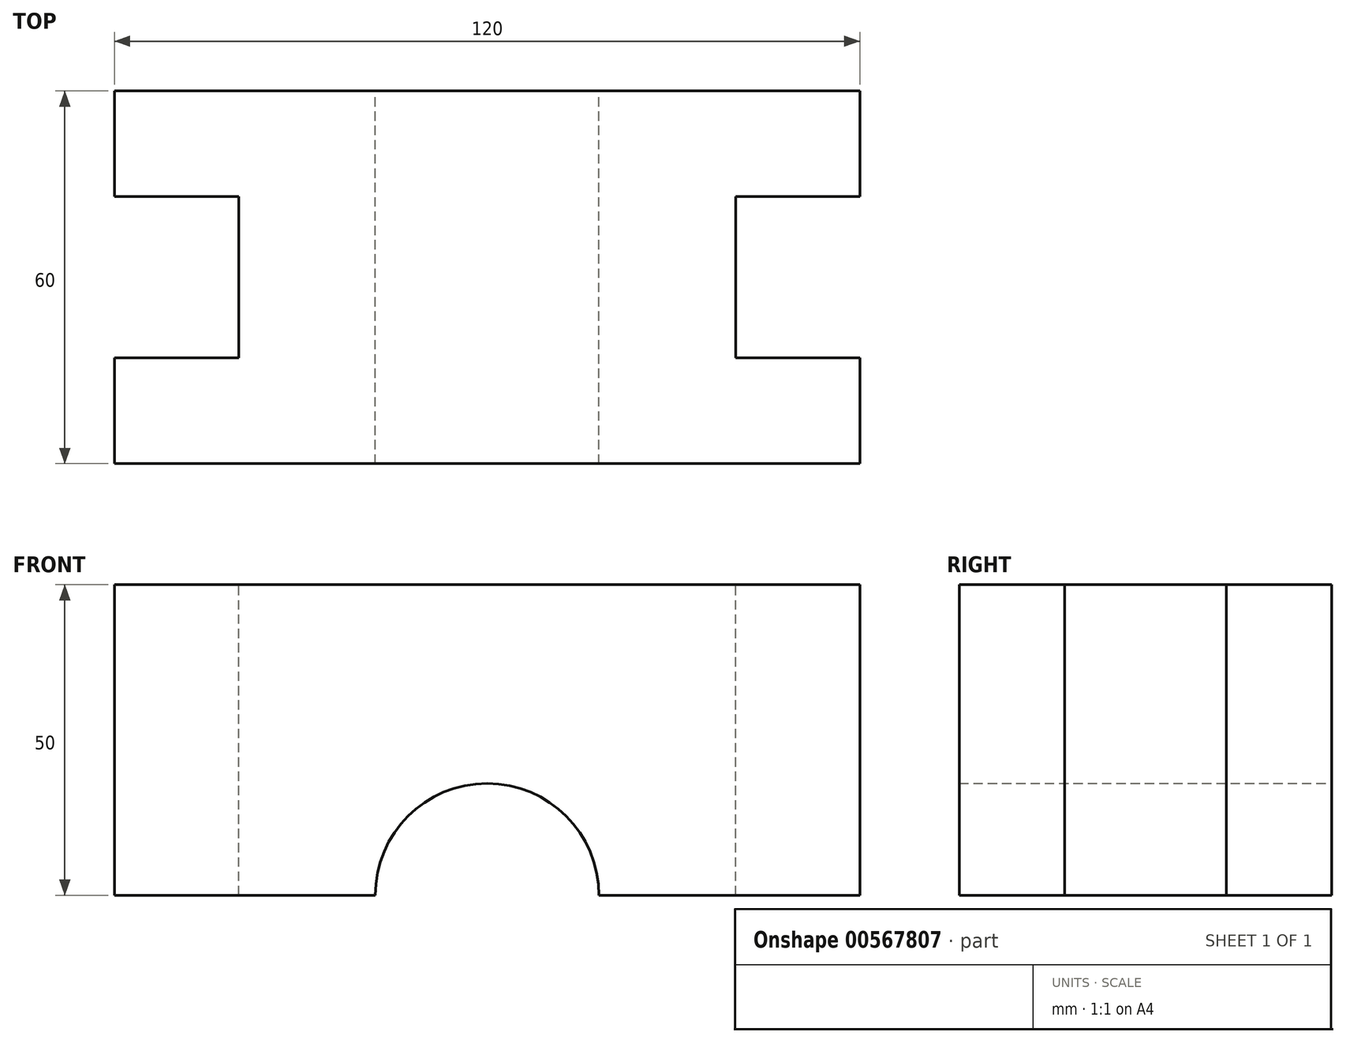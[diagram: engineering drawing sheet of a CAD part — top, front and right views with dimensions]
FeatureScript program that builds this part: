
annotation { "Feature Type Name" : "Feature", "Feature Type Description" : "" }
export const myFeature = defineFeature(function(context is Context, id is Id, definition is map)
    precondition{}
    {
        {
            var Q0;
            Q0=qCreatedBy(makeId("Front.planeOp"),FACE);
            var sketch = newSketch(context, id + "F0", { "sketchPlane" : qUnion([Q0])});
            skLineSegment(sketch, "E0.bottom", {"start": v(-60, 25) * mm, "end": v(60, 25) * mm});
            skLineSegment(sketch, "E0.top", {"start": v(-60, -25) * mm, "end": v(-18, -25) * mm});
            skLineSegment(sketch, "E0.left", {"start": v(-60, 25) * mm, "end": v(-60, -25) * mm});
            skLineSegment(sketch, "E0.right", {"start": v(60, 25) * mm, "end": v(60, -25) * mm});
            skPoint(sketch, "E0.middle", {"position": v(0, 0) * mm});
            skArc(sketch, "E1", {"start": v(18, -25) * mm, "mid": v(0, -7) * mm, "end": v(-18, -25) * mm});
            skLineSegment(sketch, "E2.trimOffspring", {"start": v(18, -25) * mm, "end": v(60, -25) * mm});
            skSolve(sketch);
        }
        {
            var Q0;
            Q0=makeQuery(id+"F0.imprint","IMPRINT",FACE,{"disambiguationData":[TD([[makeQuery(id+"F0.imprint","IMPRINT",EDGE,{"derivedFrom":sQuery(id+"F0.wireOp",EDGE,"E0.bottom")}),-1.0]])]});
            extrude(context, id + "F1", {"entities" : qUnion([Q0]), "depth" : 60 * mm, "offsetDistance" : 25 * mm});
        }
        {
            var Q0;
            Q0=makeQuery(id+"F1.opExtrude","SWEPT_FACE",FACE,{"disambiguationData":[OSD([sQuery(id+"F0.wireOp",EDGE,"E0.bottom")])]});
            var sketch = newSketch(context, id + "F2", { "sketchPlane" : qUnion([Q0])});
            skLineSegment(sketch, "E3", {"start": v(-60, 0) * mm, "end": v(-60, -17) * mm});
            skLineSegment(sketch, "E4", {"start": v(-60, -17) * mm, "end": v(-60, -43) * mm});
            skLineSegment(sketch, "E5", {"start": v(-60, -43) * mm, "end": v(-60, -60) * mm});
            skLineSegment(sketch, "E6", {"start": v(-60, -17) * mm, "end": v(-40, -17) * mm});
            skLineSegment(sketch, "E7", {"start": v(-40, -17) * mm, "end": v(-40, -43) * mm});
            skLineSegment(sketch, "E8", {"start": v(-40, -43) * mm, "end": v(-60, -43) * mm});
            skSolve(sketch);
        }
        {
            var Q0;
            Q0=makeQuery(id+"F2.imprint","IMPRINT",FACE,{"disambiguationData":[TD([[makeQuery(id+"F2.imprint","IMPRINT",EDGE,{"derivedFrom":sQuery(id+"F2.wireOp",EDGE,"E4")}),-1.0]])]});
            extrude(context, id + "F3", {"entities" : qUnion([Q0]), "operationType" : NewBodyOperationType.REMOVE, "endBound" : BoundingType.THROUGH_ALL, "oppositeDirection" : true, "depth" : 25 * mm, "offsetDistance" : 25 * mm});
        }
        {
            var Q0;
            Q0=makeQuery(id+"F1.opExtrude","SWEPT_FACE",FACE,{"disambiguationData":[OSD([sQuery(id+"F0.wireOp",EDGE,"E0.bottom")])]});
            var sketch = newSketch(context, id + "F4", { "sketchPlane" : qUnion([Q0])});
            skSolve(sketch);
        }
        {
            var Q0;
            {var subQ1=sQuery(id+"F0.wireOp",EDGE,"E0.bottom");Q0=makeQuery(id+"F4.imprint","IMPRINT",FACE,{"disambiguationData":[TD([[makeQuery(id+"F4.imprint","IMPRINT",EDGE,{"derivedFrom":makeQuery(id+"F1.opExtrude","CAP_EDGE",EDGE,{"disambiguationData":[OSD([subQ1])],"isStart":true})}),-1.0]])]});}
            var sketch = newSketch(context, id + "F5", { "sketchPlane" : qUnion([Q0])});
            skPoint(sketch, "E9.start.orphan", {"position": v(69.82, 0) * mm});
            skLineSegment(sketch, "E10.bottom", {"start": v(40, -17) * mm, "end": v(60, -17) * mm});
            skLineSegment(sketch, "E10.top", {"start": v(40, -43) * mm, "end": v(60, -43) * mm});
            skLineSegment(sketch, "E10.left", {"start": v(40, -17) * mm, "end": v(40, -43) * mm});
            skPoint(sketch, "E10.middle", {"position": v(60, -30) * mm});
            skPoint(sketch, "E10.right.start.orphan", {"position": v(80, -17) * mm});
            skPoint(sketch, "E11.orphan", {"position": v(80, -43) * mm});
            skSolve(sketch);
        }
        {
            var Q0;
            {var subQ0=sQuery(id+"F5.wireOp",EDGE,"E10.bottom");Q0=makeQuery(id+"F5.imprint","IMPRINT",FACE,{"disambiguationData":[TD([[makeQuery(id+"F5.imprint","IMPRINT",EDGE,{"derivedFrom":subQ0}),-1.0]])]});}
            extrude(context, id + "F6", {"entities" : qUnion([Q0]), "operationType" : NewBodyOperationType.REMOVE, "endBound" : BoundingType.THROUGH_ALL, "oppositeDirection" : true, "depth" : 25 * mm, "offsetDistance" : 25 * mm});
        }
    });
